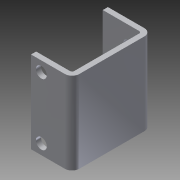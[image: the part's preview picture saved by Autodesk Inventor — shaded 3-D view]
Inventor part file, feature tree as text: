
AUTODESK INVENTOR PART (.ipt)
format: ipt  version: 2013 (Build 170138000, 138)  size: 244,736 bytes
history: native  units: in
note: dims shown in document units (in); Inventor stores cm internally (conversion verified against a paired STEP export)
features: reference x8, sheet_metal_op x7, sketch x7, other x6, extrude x2
ambient origin geometry x8: Origin, YZ Plane, XZ Plane, XY Plane, X Axis, Y Axis, Z Axis, Center Point
bodies: Solid1 (feature_tree)
feature tree (30):
  sheet_metal_op  "Face1"
  sheet_metal_op  "Flange1"
  sheet_metal_op  "Flange2"
  extrude  "Extrusion1"  Depth=2.0in
  extrude  "Extrusion2"  Depth=0.125in
  sketch  "Sketch1"  dims[d0=1.0in d1=2.0in]
  other  "Plate1"
  sketch  "Sketch2"  dims[d2=0.125in d3=0.125in]
  other  "Plate2"
  sheet_metal_op  "Bend1"
  sheet_metal_op  "Corner1"
  sketch  "Sketch3"  dims[d4=0.0625in]
  other  "Plate3"
  sheet_metal_op  "Bend2"
  sheet_metal_op  "Corner2"
  sketch  "Sketch4"  dims[d5=0.25in]
  sketch  "Sketch5"  dims[d6=0.125in]
  sketch  "Sketch6"  dims[d7=1.9375in d8=90.0deg d9=0.05in]
  reference  "Reference1"
  reference  "Reference2"
  sketch  "Sketch8"  dims[d10=0.5in d11=0.125in d12=0.125in d13=0.125in d14=0.0625in d15=0.25in d16=0.125in d17=1.0in d18=90.0deg d19=0.05in d20=0.5in d21=0.125in d22=0.125in d23=0.564in d24=0.0in d25=0.5in d26=0.0in d27=0.75in d28=0.125in d29=0.0in d32=0.125in d33=0.0in]
  reference  "Reference8"
  reference  "Reference9"
  reference  "Reference10"
  reference  "Reference11"
  reference  "Reference12"
  reference  "Reference13"
  other  "Cut1"
  other  "Cut3"
  other  "Definition1"
